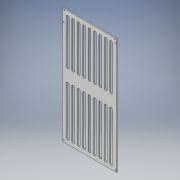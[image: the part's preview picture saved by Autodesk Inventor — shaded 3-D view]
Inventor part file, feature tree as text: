
AUTODESK INVENTOR PART (.ipt)
format: ipt  version: 2017 (Build 210142000, 142)  size: 246,272 bytes
history: native  units: in
note: dims shown in document units (in); Inventor stores cm internally (conversion verified against a paired STEP export)
features: sketch x3, extrude x2, hole x1
ambient origin geometry x8: Origin, YZ Plane, XZ Plane, XY Plane, X Axis, Y Axis, Z Axis, Center Point
bodies: Solid1 (feature_tree)
feature tree (6):
  extrude  "Extrusion1"  Depth=15.0in
  hole  "Hole1"  [1 undecoded]
  extrude  "Extrusion2"  Depth=0.3937in
  sketch  "Sketch1"  dims[d0=7.016in d1=15.0in]
  sketch  "Sketch2"  dims[d2=0.125in d3=0.0in d4=0.159in]
  sketch  "Sketch3"  dims[d5=0.25in d6=1.5in d7=90.0deg d8=0.125in d9=0.25in d10=0.125in d11=0.25in d12=0.14in d13=0.75in d14=0.375in d15=0.25in d16=0.5635in d17=1.0in d18=0.8108in d19=0.159in d21=0.125in d22=0.5in d23=0.125in d24=0.375in d27=0.5in d34=0.5in d39=15.0in d40=6.0in d41=6.5in d44=3.5433in d46=0.705in d47=0.3937in d49=1.0in d51=0.5in d52=0.3301in d53=3.5433in d55=0.7051in d56=0.3937in d58=1.0in d60=1.0in d61=0.0in]
note: 1 required parameter value undecoded (feature->parameter linkage not recoverable at this tier; creation-order binding heuristic only, values carry confidence <= 0.55)
